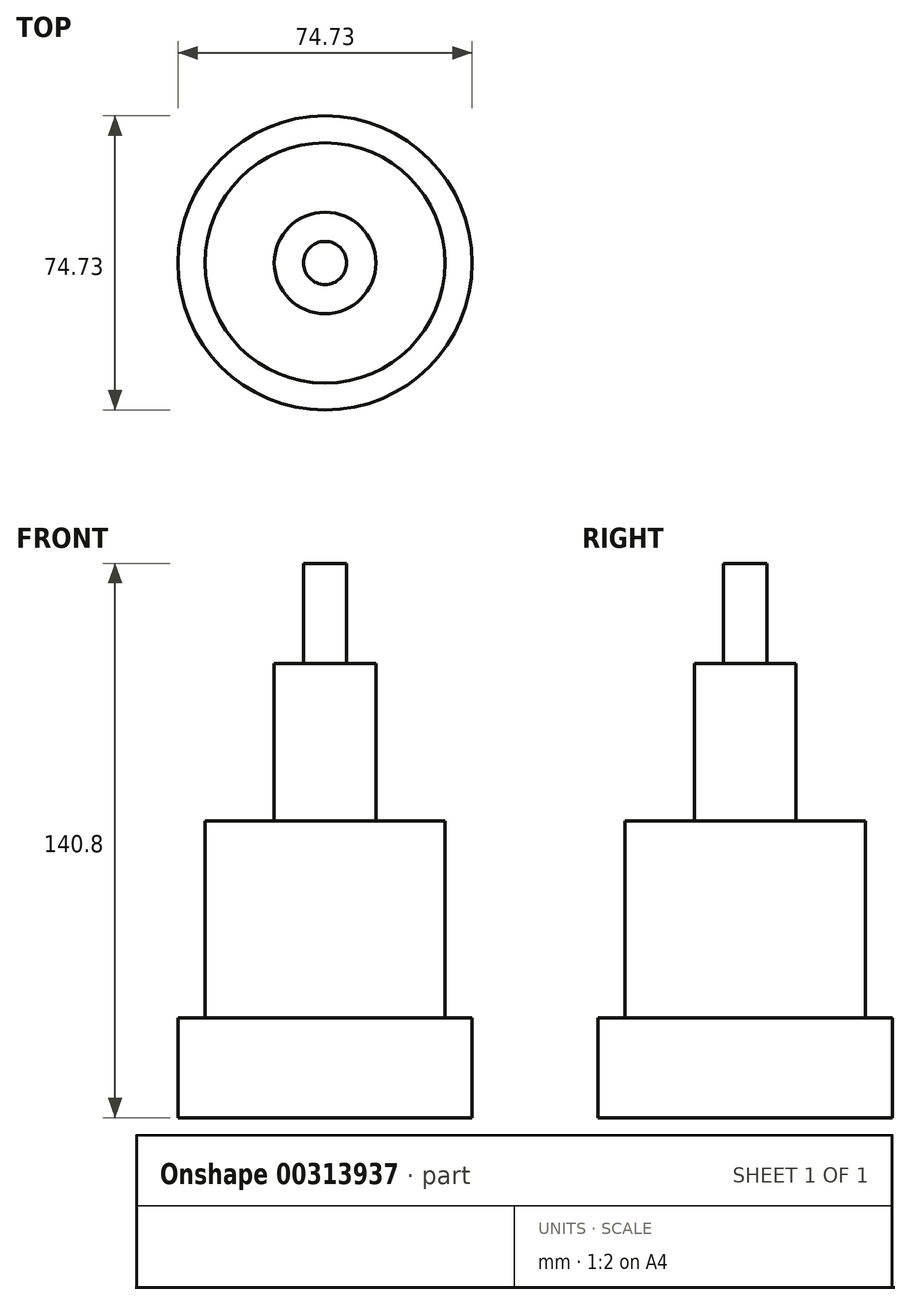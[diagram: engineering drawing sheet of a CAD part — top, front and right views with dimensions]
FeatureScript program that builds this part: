
annotation { "Feature Type Name" : "Feature", "Feature Type Description" : "" }
export const myFeature = defineFeature(function(context is Context, id is Id, definition is map)
    precondition{}
    {
        {
            var Q0;
            Q0=qCreatedBy(makeId("Top.planeOp"),FACE);
            var sketch = newSketch(context, id + "F0", { "sketchPlane" : qUnion([Q0])});
            skCircle(sketch, "E0", {"center": v(-38.14, 37.91) * mm, "radius": 37.37 * mm});
            skSolve(sketch);
        }
        {
            var Q0;
            Q0 = qSketchRegion(id + "F0", true);
            extrude(context, id + "F1", {"entities" : qUnion([Q0]), "depth" : 25.4 * mm});
        }
        {
            var Q0;
            Q0=makeQuery(id+"F1.opExtrude","CAP_FACE",FACE,{"disambiguationData":[OSD([sQuery(id+"F0.wireOp",EDGE,"E0")])],"isStart":false});
            var sketch = newSketch(context, id + "F2", { "sketchPlane" : qUnion([Q0])});
            skCircle(sketch, "E1", {"center": v(-38.14, 37.91) * mm, "radius": 30.5 * mm});
            skSolve(sketch);
        }
        {
            var Q0;
            Q0 = qSketchRegion(id + "F2", true);
            extrude(context, id + "F3", {"entities" : qUnion([Q0]), "operationType" : NewBodyOperationType.ADD, "depth" : 50 * mm});
        }
        {
            var Q0;
            Q0=makeQuery(id+"F3.opExtrude","CAP_FACE",FACE,{"disambiguationData":[OSD([sQuery(id+"F2.wireOp",EDGE,"E1")])],"isStart":false});
            var sketch = newSketch(context, id + "F4", { "sketchPlane" : qUnion([Q0])});
            skCircle(sketch, "E2", {"center": v(-38.14, 37.91) * mm, "radius": 12.9 * mm});
            skSolve(sketch);
        }
        {
            var Q0;
            Q0 = qSketchRegion(id + "F4", true);
            extrude(context, id + "F5", {"entities" : qUnion([Q0]), "operationType" : NewBodyOperationType.ADD, "depth" : 40 * mm});
        }
        {
            var Q0;
            Q0=makeQuery(id+"F5.opExtrude","CAP_FACE",FACE,{"disambiguationData":[OSD([sQuery(id+"F4.wireOp",EDGE,"E2")])],"isStart":false});
            var sketch = newSketch(context, id + "F6", { "sketchPlane" : qUnion([Q0])});
            skCircle(sketch, "E3", {"center": v(-38.14, 37.91) * mm, "radius": 5.48 * mm});
            skSolve(sketch);
        }
        {
            var Q0;
            Q0 = qSketchRegion(id + "F6", true);
            extrude(context, id + "F7", {"entities" : qUnion([Q0]), "operationType" : NewBodyOperationType.ADD, "depth" : 25.4 * mm});
        }
    });
